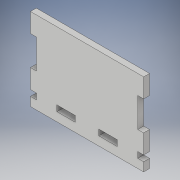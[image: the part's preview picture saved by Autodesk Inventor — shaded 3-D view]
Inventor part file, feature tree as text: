
AUTODESK INVENTOR PART (.ipt)
format: ipt  version: 2019 (Build 230136000, 136)  size: 128,000 bytes
history: native  units: mm
features: other x1, extrude x1, sketch x1
ambient origin geometry x8: Origin, YZ Plane, XZ Plane, XY Plane, X Axis, Y Axis, Z Axis, Center Point
bodies: Body1 (feature_tree)
feature tree (3):
  other  "Твердое тело1"
  extrude  "Выдавливание1"  Depth=4.0mm
  sketch  "Эскиз1"
